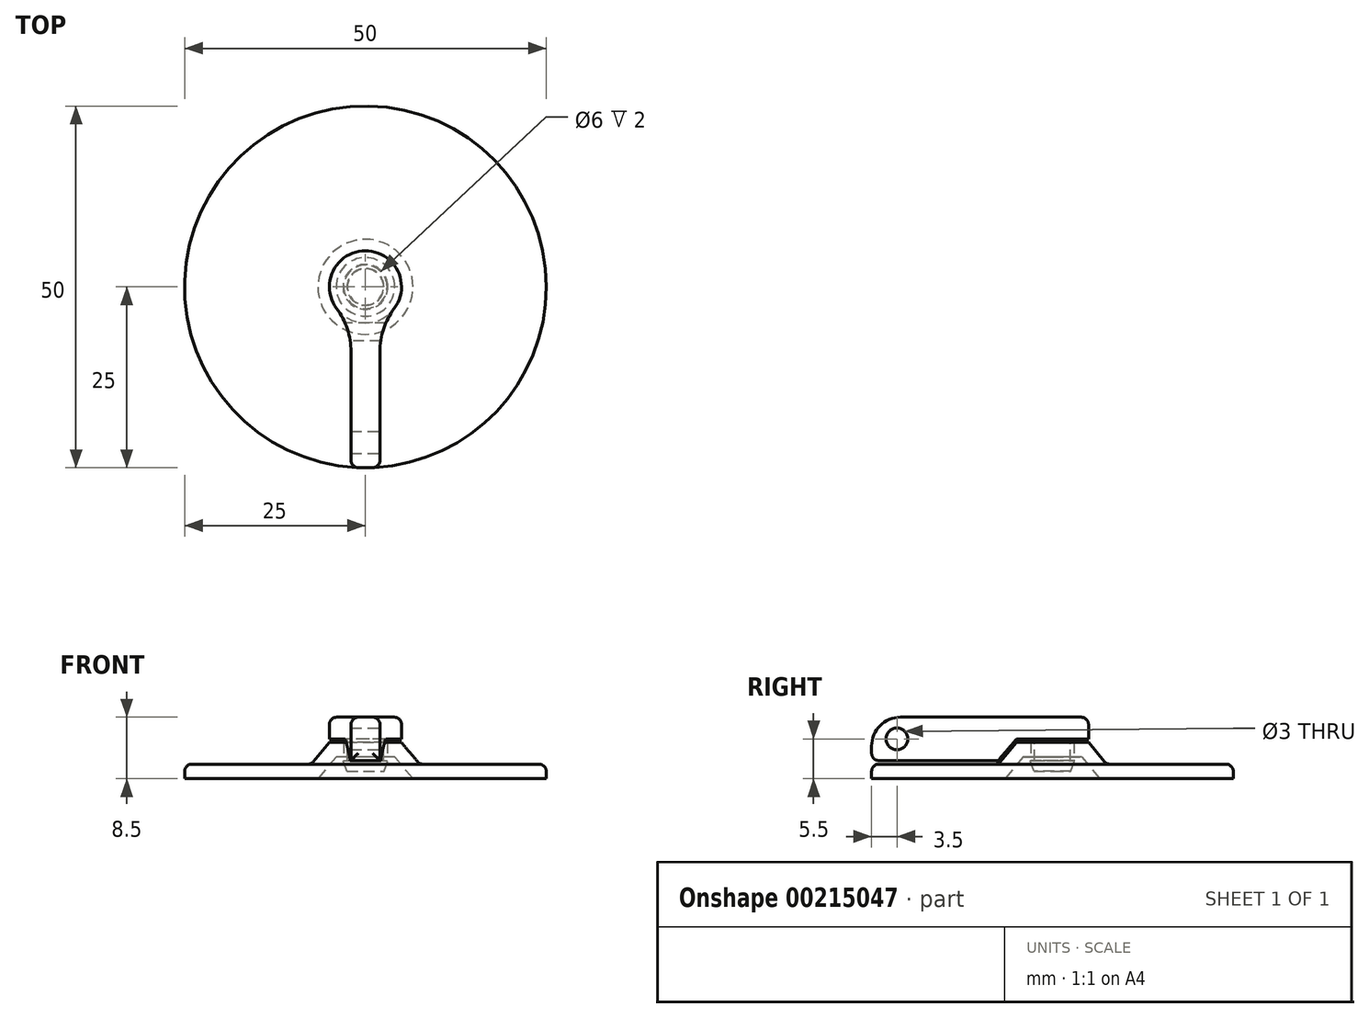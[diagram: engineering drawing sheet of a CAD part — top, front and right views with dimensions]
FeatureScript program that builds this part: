
annotation { "Feature Type Name" : "Feature", "Feature Type Description" : "" }
export const myFeature = defineFeature(function(context is Context, id is Id, definition is map)
    precondition{}
    {
        {
            var Q0;
            Q0=qCreatedBy(makeId("Top.planeOp"),FACE);
            var sketch = newSketch(context, id + "F0", { "sketchPlane" : qUnion([Q0])});
            skCircle(sketch, "E0", {"center": v(0, 0) * mm, "radius": 25 * mm});
            skSolve(sketch);
        }
        {
            var Q0;
            Q0 = qSketchRegion(id + "F0", true);
            extrude(context, id + "F1", {"entities" : qUnion([Q0]), "depth" : 2 * mm});
        }
        {
            var Q0;
            Q0=qCreatedBy(makeId("Top.planeOp"),FACE);
            var sketch = newSketch(context, id + "F2", { "sketchPlane" : qUnion([Q0])});
            skCircle(sketch, "E1", {"center": v(0, 0) * mm, "radius": 3 * mm});
            skSolve(sketch);
        }
        {
            var Q0;
            Q0=makeQuery(id+"F1.opExtrude","CAP_FACE",FACE,{"disambiguationData":[OSD([sQuery(id+"F0.wireOp",EDGE,"E0")])],"isStart":false});
            var sketch = newSketch(context, id + "F3", { "sketchPlane" : qUnion([Q0])});
            skCircle(sketch, "E2", {"center": v(0, 0) * mm, "radius": 7.5 * mm});
            skSolve(sketch);
        }
        {
            var Q0;
            Q0 = qSketchRegion(id + "F3", true);
            extrude(context, id + "F4", {"entities" : qUnion([Q0]), "operationType" : NewBodyOperationType.ADD, "depth" : 3 * mm, "hasDraft" : true, "draftAngle" : 40 * degree, "draftPullDirection" : true});
        }
        {
            var Q0;
            Q0=makeQuery(id+"F1.opExtrude","CAP_FACE",FACE,{"disambiguationData":[OSD([sQuery(id+"F0.wireOp",EDGE,"E0")])],"isStart":true});
            shell(context, id + "F5", {"entities" : qUnion([Q0]), "thickness" : 2 * mm});
        }
        {
            var Q0;
            Q0=makeQuery(id+"F2.imprint","IMPRINT",FACE,{"disambiguationData":[TD([[makeQuery(id+"F2.imprint","IMPRINT",EDGE,{"derivedFrom":sQuery(id+"F2.wireOp",EDGE,"E1")}),1.0]])]});
            extrude(context, id + "F6", {"entities" : qUnion([Q0]), "operationType" : NewBodyOperationType.REMOVE, "endBound" : BoundingType.THROUGH_ALL, "depth" : 25 * mm});
        }
        {
            var Q0;
            Q0=makeQuery(id+"F4.opExtrude","CAP_FACE",FACE,{"disambiguationData":[OSD([sQuery(id+"F3.wireOp",EDGE,"E2")])],"isStart":false});
            cPlane(context, id + "F7", {"entities" : qUnion([Q0]), "cplaneType" : CPlaneType.OFFSET, "offset" : .5 * mm, "width" : 150 * mm, "height" : 150 * mm});
        }
        {
            var Q0;
            Q0=qCreatedBy(id+"F7.planeOp",FACE);
            var sketch = newSketch(context, id + "F8", { "sketchPlane" : qUnion([Q0])});
            skCircle(sketch, "E3", {"center": v(0, 0) * mm, "radius": 2.5 * mm});
            skSolve(sketch);
        }
        {
            var Q0;
            Q0 = qSketchRegion(id + "F8", true);
            extrude(context, id + "F9", {"entities" : qUnion([Q0]), "oppositeDirection" : true, "depth" : 3 * mm});
        }
        {
            var Q0;
            Q0=makeQuery(id+"F9.opExtrude","CAP_FACE",FACE,{"disambiguationData":[OSD([sQuery(id+"F8.wireOp",EDGE,"E3")])],"isStart":false});
            var sketch = newSketch(context, id + "F10", { "sketchPlane" : qUnion([Q0])});
            skCircle(sketch, "E4", {"center": v(0, 0) * mm, "radius": 3.1 * mm});
            skSolve(sketch);
        }
        {
            var Q0;
            Q0 = qSketchRegion(id + "F10", true);
            extrude(context, id + "F11", {"entities" : qUnion([Q0]), "operationType" : NewBodyOperationType.ADD, "depth" : 1.5 * mm, "hasDraft" : true, "draftAngle" : 20 * degree, "draftPullDirection" : true});
        }
        {
            var Q0;
            Q0=qCreatedBy(makeId("Right.planeOp"),FACE);
            var sketch = newSketch(context, id + "F12", { "sketchPlane" : qUnion([Q0])});
            skLineSegment(sketch, "E5.0", {"start": v(-2.5, 5.5) * mm, "end": v(2.5, 5.5) * mm});
            skLineSegment(sketch, "E6.0", {"start": v(-4.98, 5) * mm, "end": v(4.98, 5) * mm, "construction": true});
            skLineSegment(sketch, "E7.0", {"start": v(-25, 2) * mm, "end": v(25, 2) * mm, "construction": true});
            skLineSegment(sketch, "E8.0", {"start": v(-7.5, 2) * mm, "end": v(7.5, 2) * mm, "construction": true});
            skLineSegment(sketch, "E9.0", {"start": v(-25, 2.5) * mm, "end": v(25, 2.5) * mm, "construction": true});
            skLineSegment(sketch, "E10.0", {"start": v(-7.5, 2.5) * mm, "end": v(7.5, 2.5) * mm, "construction": true});
            skLineSegment(sketch, "E11.0", {"start": v(-4.98, 5.5) * mm, "end": v(4.98, 5.5) * mm, "construction": true});
            skLineSegment(sketch, "E12", {"start": v(-4.98, 5.5) * mm, "end": v(-7.5, 2.5) * mm});
            skLineSegment(sketch, "E13", {"start": v(-25, 2.5) * mm, "end": v(-25, 8.5) * mm});
            skLineSegment(sketch, "E14", {"start": v(-25, 2.5) * mm, "end": v(-7.5, 2.5) * mm});
            skLineSegment(sketch, "E15", {"start": v(4.98, 5.5) * mm, "end": v(4.98, 8.5) * mm, "construction": true});
            skLineSegment(sketch, "E16", {"start": v(4.98, 8.5) * mm, "end": v(-25, 8.5) * mm, "construction": true});
            skLineSegment(sketch, "E17", {"start": v(0, 5.5) * mm, "end": v(0, 8.5) * mm, "construction": true});
            skLineSegment(sketch, "E18", {"start": v(-4.98, 5.5) * mm, "end": v(0, 5.5) * mm});
            skLineSegment(sketch, "E19", {"start": v(0, 8.5) * mm, "end": v(-25, 8.5) * mm});
            skLineSegment(sketch, "E20", {"start": v(0, 8.5) * mm, "end": v(0, 5.5) * mm});
            skSolve(sketch);
        }
        {
            var Q0;
            Q0=qCreatedBy(id+"F7.planeOp",FACE);
            var sketch = newSketch(context, id + "F13", { "sketchPlane" : qUnion([Q0])});
            skCircle(sketch, "E21.0", {"center": v(0, 0) * mm, "radius": 4.98 * mm});
            skSolve(sketch);
        }
        {
            var Q0;
            Q0 = qSketchRegion(id + "F13", true);
            extrude(context, id + "F14", {"entities" : qUnion([Q0]), "operationType" : NewBodyOperationType.ADD, "depth" : 3 * mm});
        }
        {
            var Q0;
            Q0 = qSketchRegion(id + "F12", true);
            extrude(context, id + "F15", {"entities" : qUnion([Q0]), "operationType" : NewBodyOperationType.ADD, "endBound" : BoundingType.SYMMETRIC, "depth" : 4 * mm});
        }
        {
            var Q0;
            Q0=makeQuery(id+"F15.boolean.opBoolean","INTERSECT",EDGE,{"derivedFrom":[makeQuery(id+"F14.opExtrude","SWEPT_FACE",FACE,{"disambiguationData":[OSD([sQuery(id+"F13.wireOp",EDGE,"E21.0")])]}),makeQuery(id+"F15.opExtrude","CAP_FACE",FACE,{"disambiguationData":[OSD([sQuery(id+"F12.wireOp",EDGE,"E12"),sQuery(id+"F12.wireOp",EDGE,"E13"),sQuery(id+"F12.wireOp",EDGE,"E14"),sQuery(id+"F12.wireOp",EDGE,"E18"),sQuery(id+"F12.wireOp",EDGE,"E19"),sQuery(id+"F12.wireOp",EDGE,"E20")])],"isStart":false})]});
            var Q1;
            Q1=makeQuery(id+"F15.boolean.opBoolean","INTERSECT",EDGE,{"derivedFrom":[makeQuery(id+"F14.opExtrude","SWEPT_FACE",FACE,{"disambiguationData":[OSD([sQuery(id+"F13.wireOp",EDGE,"E21.0")])]}),makeQuery(id+"F15.opExtrude","CAP_FACE",FACE,{"disambiguationData":[OSD([sQuery(id+"F12.wireOp",EDGE,"E12"),sQuery(id+"F12.wireOp",EDGE,"E13"),sQuery(id+"F12.wireOp",EDGE,"E14"),sQuery(id+"F12.wireOp",EDGE,"E18"),sQuery(id+"F12.wireOp",EDGE,"E19"),sQuery(id+"F12.wireOp",EDGE,"E20")])],"isStart":true})]});
            fillet(context, id + "F16", {"entities" : qUnion([Q0, Q1]), "radius" : 10 * mm, "tangentPropagation" : true, "allowEdgeOverflow" : false});
        }
        {
            var Q0;
            Q0=makeQuery(id+"F15.opExtrude","SWEPT_EDGE",EDGE,{"disambiguationData":[OSD([sQuery(id+"F12.wireOp",EDGE,"E13"),sQuery(id+"F12.wireOp",EDGE,"E19")])]});
            fillet(context, id + "F17", {"entities" : qUnion([Q0]), "radius" : 4 * mm, "tangentPropagation" : true, "allowEdgeOverflow" : false});
        }
        {
            var Q0;
            Q0=makeQuery(id+"F15.opExtrude","CAP_FACE",FACE,{"disambiguationData":[OSD([sQuery(id+"F12.wireOp",EDGE,"E12"),sQuery(id+"F12.wireOp",EDGE,"E13"),sQuery(id+"F12.wireOp",EDGE,"E14"),sQuery(id+"F12.wireOp",EDGE,"E18"),sQuery(id+"F12.wireOp",EDGE,"E19"),sQuery(id+"F12.wireOp",EDGE,"E20")])],"isStart":false});
            var sketch = newSketch(context, id + "F18", { "sketchPlane" : qUnion([Q0])});
            skCircle(sketch, "E22", {"center": v(-21.5, 5.5) * mm, "radius": 1.5 * mm});
            skSolve(sketch);
        }
        {
            var Q0;
            Q0=makeQuery(id+"F18.imprint","IMPRINT",FACE,{"disambiguationData":[TD([[makeQuery(id+"F18.imprint","IMPRINT",EDGE,{"derivedFrom":sQuery(id+"F18.wireOp",EDGE,"E22")}),1.0]])]});
            extrude(context, id + "F19", {"entities" : qUnion([Q0]), "operationType" : NewBodyOperationType.REMOVE, "endBound" : BoundingType.THROUGH_ALL, "oppositeDirection" : true, "depth" : 25 * mm});
        }
        {
            var Q0;
            Q0=makeQuery(id+"F15.boolean.opBoolean","MERGE",FACE,{"derivedFrom":[makeQuery(id+"F14.opExtrude","CAP_FACE",FACE,{"disambiguationData":[OSD([sQuery(id+"F13.wireOp",EDGE,"E21.0")])],"isStart":false}),makeQuery(id+"F15.opExtrude","SWEPT_FACE",FACE,{"disambiguationData":[OSD([sQuery(id+"F12.wireOp",EDGE,"E19")])]})]});
            var Q1;
            Q1=makeQuery(id+"F17.opFillet","BLEND_FACE",FACE,{"disambiguationData":[OSD([sQuery(id+"F12.wireOp",EDGE,"E13"),sQuery(id+"F12.wireOp",EDGE,"E19")])]});
            var Q2;
            Q2=makeQuery(id+"F15.opExtrude","SWEPT_FACE",FACE,{"disambiguationData":[OSD([sQuery(id+"F12.wireOp",EDGE,"E13")])]});
            fillet(context, id + "F20", {"entities" : qUnion([Q0, Q1, Q2]), "radius" : 1 * mm, "tangentPropagation" : true, "allowEdgeOverflow" : false});
        }
        {
            var Q0;
            Q0=makeQuery(id+"F1.opExtrude","CAP_FACE",FACE,{"disambiguationData":[OSD([sQuery(id+"F0.wireOp",EDGE,"E0")])],"isStart":false});
            fillet(context, id + "F21", {"entities" : qUnion([Q0]), "radius" : 1 * mm, "tangentPropagation" : true, "allowEdgeOverflow" : false});
        }
    });
